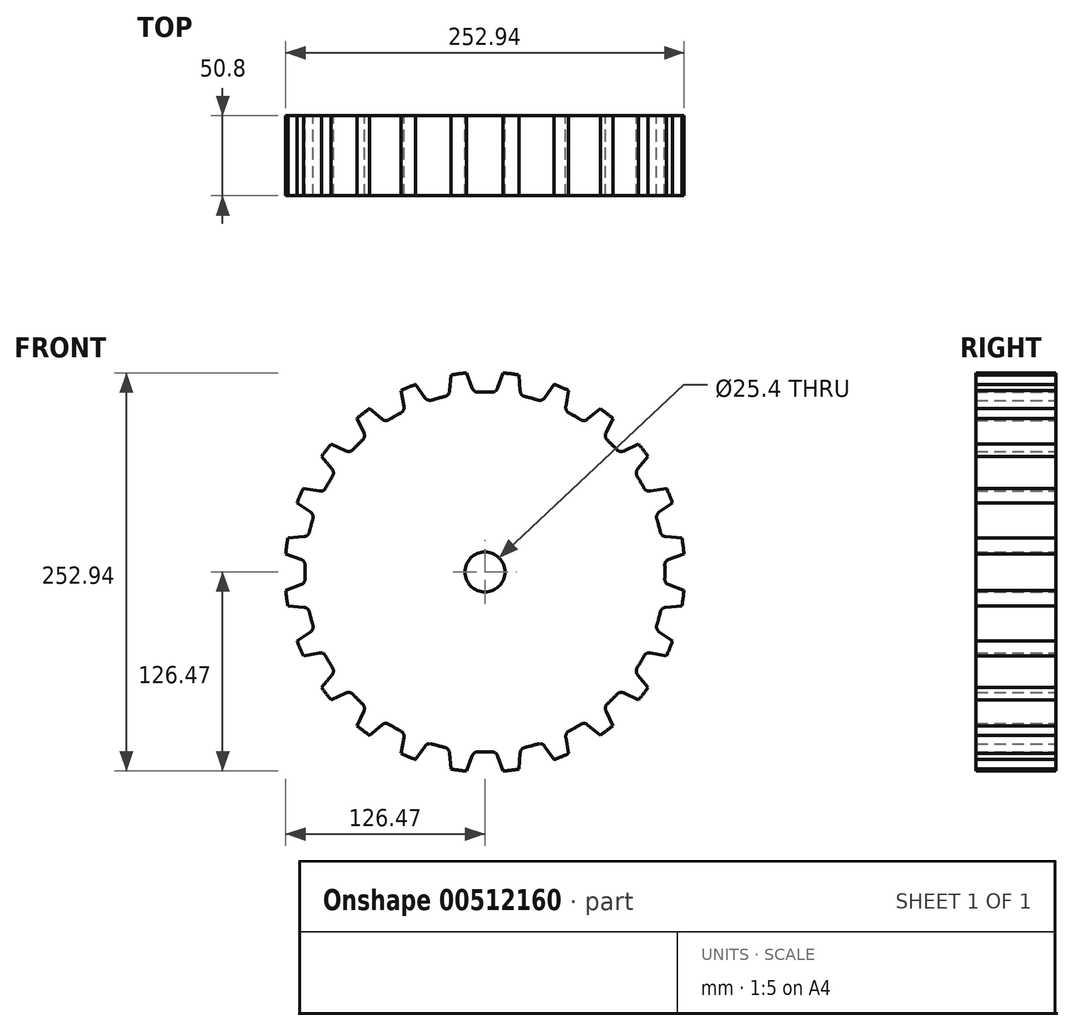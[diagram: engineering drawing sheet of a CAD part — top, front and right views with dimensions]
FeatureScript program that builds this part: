
annotation { "Feature Type Name" : "Feature", "Feature Type Description" : "" }
export const myFeature = defineFeature(function(context is Context, id is Id, definition is map)
    precondition{}
    {
        {
            var Q0;
            Q0=qCreatedBy(makeId("Front.planeOp"),FACE);
            var sketch = newSketch(context, id + "F0", { "sketchPlane" : qUnion([Q0])});
            skCircle(sketch, "E0", {"center": v(0, 0) * mm, "radius": 127 * mm});
            skCircle(sketch, "E1", {"center": v(0, 0) * mm, "radius": 12.7 * mm});
            skSolve(sketch);
        }
        {
            var Q0;
            Q0 = qSketchRegion(id + "F0", true);
            extrude(context, id + "F1", {"entities" : qUnion([Q0]), "endBound" : BoundingType.SYMMETRIC, "depth" : 50.8 * mm});
        }
        {
            var Q0;
            Q0=qCreatedBy(makeId("Front.planeOp"),FACE);
            var sketch = newSketch(context, id + "F2", { "sketchPlane" : qUnion([Q0])});
            skArc(sketch, "E2", {"start": v(11.6, 126.47) * mm, "mid": v(0, 127) * mm, "end": v(-11.6, 126.47) * mm});
            skArc(sketch, "E3", {"start": v(4.32, 114.22) * mm, "mid": v(0, 114.3) * mm, "end": v(-4.32, 114.22) * mm});
            skLineSegment(sketch, "E4", {"start": v(0, 0) * mm, "end": v(0, 159.07) * mm, "construction": true});
            skLineSegment(sketch, "E5", {"start": v(8.05, 116.72) * mm, "end": v(11.6, 126.47) * mm});
            skLineSegment(sketch, "E6.MirrorCS", {"start": v(-8.05, 116.72) * mm, "end": v(-11.6, 126.47) * mm});
            skPoint(sketch, "E7.visualSharp", {"position": v(-7.08, 114.08) * mm});
            skArc(sketch, "E7.filletArc", {"start": v(-8.05, 116.72) * mm, "mid": v(-6.6, 114.86) * mm, "end": v(-4.32, 114.22) * mm});
            skPoint(sketch, "E8.visualSharp", {"position": v(7.08, 114.08) * mm});
            skArc(sketch, "E8.filletArc", {"start": v(4.32, 114.22) * mm, "mid": v(6.6, 114.86) * mm, "end": v(8.05, 116.72) * mm});
            skSolve(sketch);
        }
        {
            var Q0;
            Q0 = qSketchRegion(id + "F2", true);
            extrude(context, id + "F3", {"entities" : qUnion([Q0]), "operationType" : NewBodyOperationType.REMOVE, "endBound" : BoundingType.SYMMETRIC, "depth" : 50.8 * mm});
        }
        {
            var Q0;
            Q0=makeQuery(id+"F3.boolean.opBoolean","COPY",FACE,{"derivedFrom":makeQuery(id+"F3.opExtrude","SWEPT_FACE",FACE,{"disambiguationData":[OSD([sQuery(id+"F2.wireOp",EDGE,"E6.MirrorCS")])]})});
            var Q1;
            Q1=makeQuery(id+"F3.boolean.opBoolean","COPY",FACE,{"derivedFrom":makeQuery(id+"F3.opExtrude","SWEPT_FACE",FACE,{"disambiguationData":[OSD([sQuery(id+"F2.wireOp",EDGE,"E7.filletArc")])]})});
            var Q2;
            Q2=makeQuery(id+"F3.boolean.opBoolean","COPY",FACE,{"derivedFrom":makeQuery(id+"F3.opExtrude","SWEPT_FACE",FACE,{"disambiguationData":[OSD([sQuery(id+"F2.wireOp",EDGE,"E3")])]})});
            var Q3;
            Q3=makeQuery(id+"F3.boolean.opBoolean","COPY",FACE,{"derivedFrom":makeQuery(id+"F3.opExtrude","SWEPT_FACE",FACE,{"disambiguationData":[OSD([sQuery(id+"F2.wireOp",EDGE,"E8.filletArc")])]})});
            var Q4;
            Q4=makeQuery(id+"F3.boolean.opBoolean","COPY",FACE,{"derivedFrom":makeQuery(id+"F3.opExtrude","SWEPT_FACE",FACE,{"disambiguationData":[OSD([sQuery(id+"F2.wireOp",EDGE,"E5")])]})});
            var Q5;
            Q5=makeQuery(id+"F1.opExtrude","SWEPT_FACE",FACE,{"disambiguationData":[OSD([sQuery(id+"F0.wireOp",EDGE,"E0")])]});
            circularPattern(context, id + "F4", {"patternType" : PatternType.FACE, "faces" : qUnion([Q0, Q1, Q2, Q3, Q4]), "axis" : qUnion([Q5]), "angle" : 360 * degree, "instanceCount" : 24, "equalSpace" : true});
        }
    });
